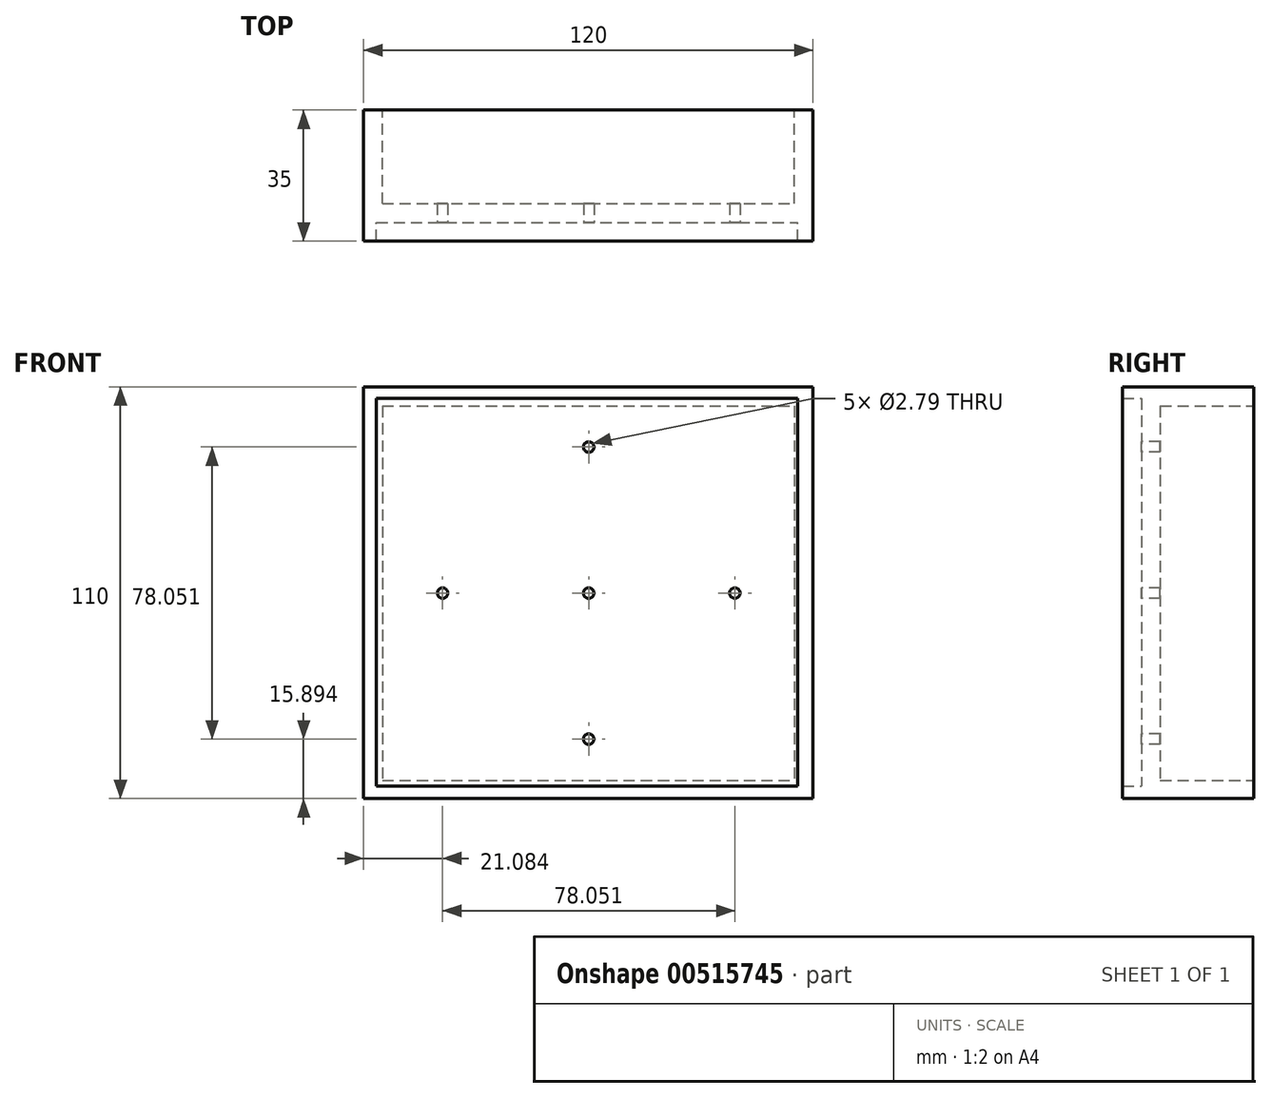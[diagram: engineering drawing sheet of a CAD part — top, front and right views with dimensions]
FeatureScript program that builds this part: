
annotation { "Feature Type Name" : "Feature", "Feature Type Description" : "" }
export const myFeature = defineFeature(function(context is Context, id is Id, definition is map)
    precondition{}
    {
        {
            var Q0;
            Q0=qCreatedBy(makeId("Front.planeOp"),FACE);
            var sketch = newSketch(context, id + "F0", { "sketchPlane" : qUnion([Q0])});
            skLineSegment(sketch, "E0.bottom", {"start": v(-60.11, 55.08) * mm, "end": v(59.89, 55.08) * mm});
            skLineSegment(sketch, "E0.top", {"start": v(-60.11, -54.92) * mm, "end": v(59.89, -54.92) * mm});
            skLineSegment(sketch, "E0.left", {"start": v(-60.11, 55.08) * mm, "end": v(-60.11, -54.92) * mm});
            skLineSegment(sketch, "E0.right", {"start": v(59.89, 55.08) * mm, "end": v(59.89, -54.92) * mm});
            skLineSegment(sketch, "E1.bottom", {"start": v(-55.11, 49.98) * mm, "end": v(54.89, 49.98) * mm});
            skLineSegment(sketch, "E1.top", {"start": v(-55.11, -50.02) * mm, "end": v(54.89, -50.02) * mm});
            skLineSegment(sketch, "E1.left", {"start": v(-55.11, 49.98) * mm, "end": v(-55.11, -50.02) * mm});
            skLineSegment(sketch, "E1.right", {"start": v(54.89, 49.98) * mm, "end": v(54.89, -50.02) * mm});
            skSolve(sketch);
        }
        {
            var Q0;
            Q0=makeQuery(id+"F0.imprint","IMPRINT",FACE,{"disambiguationData":[TD([[makeQuery(id+"F0.imprint","IMPRINT",EDGE,{"derivedFrom":sQuery(id+"F0.wireOp",EDGE,"E0.bottom")}),-1.0]])]});
            extrude(context, id + "F1", {"entities" : qUnion([Q0]), "depth" : 25 * mm, "offsetDistance" : 25 * mm});
        }
        {
            var Q0;
            Q0=makeQuery(id+"F1.opExtrude","CAP_FACE",FACE,{"disambiguationData":[OSD([sQuery(id+"F0.wireOp",EDGE,"E0.bottom"),sQuery(id+"F0.wireOp",EDGE,"E0.top"),sQuery(id+"F0.wireOp",EDGE,"E0.left"),sQuery(id+"F0.wireOp",EDGE,"E0.right"),sQuery(id+"F0.wireOp",EDGE,"E1.bottom"),sQuery(id+"F0.wireOp",EDGE,"E1.top"),sQuery(id+"F0.wireOp",EDGE,"E1.left"),sQuery(id+"F0.wireOp",EDGE,"E1.right")])],"isStart":false});
            var sketch = newSketch(context, id + "F2", { "sketchPlane" : qUnion([Q0])});
            skLineSegment(sketch, "E2.bottom", {"start": v(-60.11, 55.08) * mm, "end": v(59.89, 55.08) * mm});
            skLineSegment(sketch, "E2.top", {"start": v(-60.11, -54.92) * mm, "end": v(59.89, -54.92) * mm});
            skLineSegment(sketch, "E2.left", {"start": v(-60.11, 55.08) * mm, "end": v(-60.11, -54.92) * mm});
            skLineSegment(sketch, "E2.right", {"start": v(59.89, 55.08) * mm, "end": v(59.89, -54.92) * mm});
            skSolve(sketch);
        }
        {
            var Q0;
            Q0=makeQuery(id+"F2.imprint","IMPRINT",FACE,{"disambiguationData":[TD([[makeQuery(id+"F2.imprint","IMPRINT",EDGE,{"derivedFrom":sQuery(id+"F2.wireOp",EDGE,"E2.bottom")}),-1.0]])]});
            var Q1;
            Q1=makeQuery(id+"F2.imprint","IMPRINT",FACE,{"disambiguationData":[TD([[makeQuery(id+"F2.imprint","IMPRINT",EDGE,{"derivedFrom":makeQuery(id+"F1.opExtrude","CAP_EDGE",EDGE,{"disambiguationData":[OSD([sQuery(id+"F0.wireOp",EDGE,"E1.bottom")])],"isStart":false})}),-1.0]])]});
            extrude(context, id + "F3", {"entities" : qUnion([Q0, Q1]), "operationType" : NewBodyOperationType.ADD, "depth" : 5 * mm, "offsetDistance" : 25 * mm});
        }
        {
            var Q0;
            Q0=makeQuery(id+"F3.opExtrude","CAP_FACE",FACE,{"disambiguationData":[OSD([sQuery(id+"F2.wireOp",EDGE,"E2.bottom"),sQuery(id+"F2.wireOp",EDGE,"E2.top"),sQuery(id+"F2.wireOp",EDGE,"E2.left"),sQuery(id+"F2.wireOp",EDGE,"E2.right")])],"isStart":false});
            var sketch = newSketch(context, id + "F4", { "sketchPlane" : qUnion([Q0])});
            skLineSegment(sketch, "E3.bottom", {"start": v(-60.11, 55.08) * mm, "end": v(59.89, 55.08) * mm});
            skLineSegment(sketch, "E3.top", {"start": v(-60.11, -54.92) * mm, "end": v(59.89, -54.92) * mm});
            skLineSegment(sketch, "E3.left", {"start": v(-60.11, 55.08) * mm, "end": v(-60.11, -54.92) * mm});
            skLineSegment(sketch, "E3.right", {"start": v(59.89, 55.08) * mm, "end": v(59.89, -54.92) * mm});
            skLineSegment(sketch, "E4.bottom", {"start": v(-56.68, 52.02) * mm, "end": v(55.81, 52.02) * mm});
            skLineSegment(sketch, "E4.top", {"start": v(-56.68, -51.65) * mm, "end": v(55.81, -51.65) * mm});
            skLineSegment(sketch, "E4.left", {"start": v(-56.68, 52.02) * mm, "end": v(-56.68, -51.65) * mm});
            skLineSegment(sketch, "E4.right", {"start": v(55.81, 52.02) * mm, "end": v(55.81, -51.65) * mm});
            skSolve(sketch);
        }
        {
            var Q0;
            Q0=makeQuery(id+"F4.imprint","IMPRINT",FACE,{"disambiguationData":[TD([[makeQuery(id+"F4.imprint","IMPRINT",EDGE,{"derivedFrom":sQuery(id+"F4.wireOp",EDGE,"E3.bottom")}),-1.0]])]});
            extrude(context, id + "F5", {"entities" : qUnion([Q0]), "operationType" : NewBodyOperationType.ADD, "depth" : 5 * mm, "offsetDistance" : 25 * mm});
        }
        {
            var Q0;
            Q0=makeQuery(id+"F3.opExtrude","CAP_FACE",FACE,{"disambiguationData":[OSD([sQuery(id+"F2.wireOp",EDGE,"E2.bottom"),sQuery(id+"F2.wireOp",EDGE,"E2.top"),sQuery(id+"F2.wireOp",EDGE,"E2.left"),sQuery(id+"F2.wireOp",EDGE,"E2.right")])],"isStart":false});
            var sketch = newSketch(context, id + "F6", { "sketchPlane" : qUnion([Q0])});
            skCircle(sketch, "E5", {"center": v(0, 0) * mm, "radius": 39.03 * mm});
            skPoint(sketch, "E6", {"position": v(0, 39.03) * mm});
            skPoint(sketch, "E7", {"position": v(0, -39.03) * mm});
            skPoint(sketch, "E8", {"position": v(39.03, 0) * mm});
            skPoint(sketch, "E9", {"position": v(-39.03, 0) * mm});
            skSolve(sketch);
        }
        {
            var Q0;
            Q0=sQuery(id+"F6.wireOp",VERTEX,"E6");
            var Q1;
            Q1=sQuery(id+"F6.wireOp",VERTEX,"E9");
            var Q2;
            Q2=sQuery(id+"F6.wireOp",VERTEX,"E7");
            var Q3;
            Q3=sQuery(id+"F6.wireOp",VERTEX,"E8");
            var Q4;
            Q4=sQuery(id+"F6.wireOp",VERTEX,"E5.center");
            var Q5;
            Q5=makeQuery(id+"F1.opExtrude","SWEPT_BODY",BODY,{"disambiguationData":[OSD([sQuery(id+"F0.wireOp",EDGE,"E0.bottom"),sQuery(id+"F0.wireOp",EDGE,"E0.top"),sQuery(id+"F0.wireOp",EDGE,"E0.left"),sQuery(id+"F0.wireOp",EDGE,"E0.right"),sQuery(id+"F0.wireOp",EDGE,"E1.bottom"),sQuery(id+"F0.wireOp",EDGE,"E1.top"),sQuery(id+"F0.wireOp",EDGE,"E1.left"),sQuery(id+"F0.wireOp",EDGE,"E1.right")])]});
            hole(context, id + "F7", {"style" : HoleStyle.SIMPLE, "endStyle" : HoleEndStyle.THROUGH, "standardTappedOrClearance" : lookupTablePath({ "standard" : "ANSI", "fit" : "Normal (ASME)", "size" : "#3", "type" : "Clearance" }), "standardBlindInLast" : lookupTablePath({ "fit" : "Free", "standard" : "ANSI", "size" : "#3", "type" : "Clearance" }), "holeDiameter" : 2.8 * mm, "isTappedThrough" : true, "tappedDepth" : 12.7 * mm, "tapClearance" : 3, "locations" : qUnion([Q0, Q1, Q2, Q3, Q4]), "scope" : qUnion([Q5])});
        }
    });
